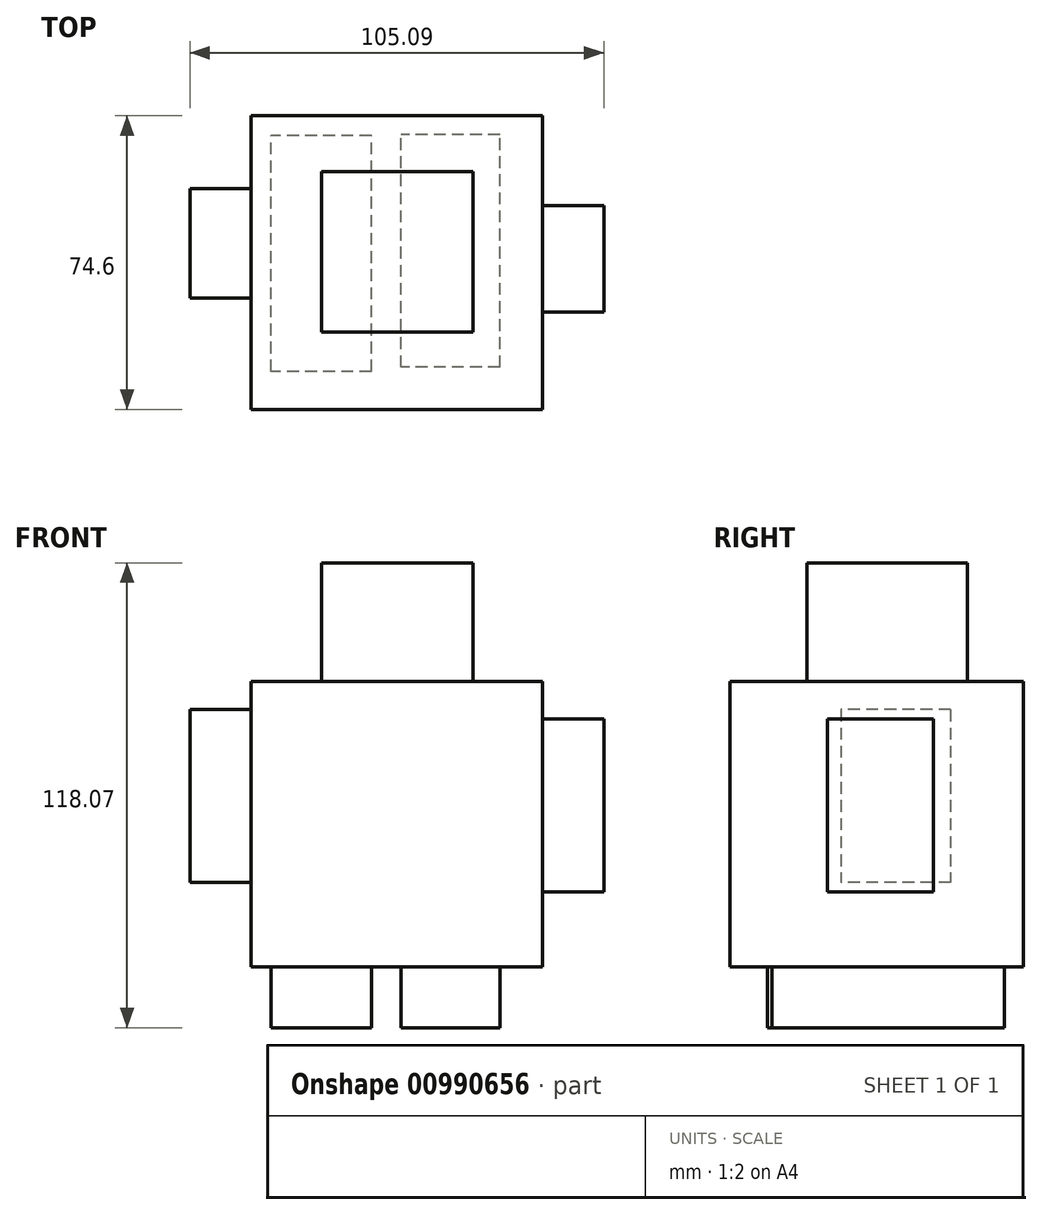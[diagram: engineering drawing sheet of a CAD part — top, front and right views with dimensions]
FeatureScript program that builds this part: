
annotation { "Feature Type Name" : "Feature", "Feature Type Description" : "" }
export const myFeature = defineFeature(function(context is Context, id is Id, definition is map)
    precondition{}
    {
        {
            var Q0;
            Q0=qCreatedBy(makeId("Top.planeOp"),FACE);
            var sketch = newSketch(context, id + "F0", { "sketchPlane" : qUnion([Q0])});
            skLineSegment(sketch, "E0.bottom", {"start": v(0, 0) * mm, "end": v(-74.1, 0) * mm});
            skLineSegment(sketch, "E0.top", {"start": v(0, 74.6) * mm, "end": v(-74.1, 74.6) * mm});
            skLineSegment(sketch, "E0.left", {"start": v(0, 0) * mm, "end": v(0, 74.6) * mm});
            skLineSegment(sketch, "E0.right", {"start": v(-74.1, 0) * mm, "end": v(-74.1, 74.6) * mm});
            skSolve(sketch);
        }
        {
            var Q0;
            Q0 = qSketchRegion(id + "F0", true);
            extrude(context, id + "F1", {"entities" : qUnion([Q0]), "depth" : 72.47 * mm, "offsetDistance" : 25.4 * mm});
        }
        {
            var Q0;
            Q0=makeQuery(id+"F1.opExtrude","CAP_FACE",FACE,{"disambiguationData":[OSD([sQuery(id+"F0.wireOp",EDGE,"E0.bottom"),sQuery(id+"F0.wireOp",EDGE,"E0.top"),sQuery(id+"F0.wireOp",EDGE,"E0.left"),sQuery(id+"F0.wireOp",EDGE,"E0.right")])],"isStart":false});
            var sketch = newSketch(context, id + "F2", { "sketchPlane" : qUnion([Q0])});
            skLineSegment(sketch, "E1.bottom", {"start": v(-56.15, 60.44) * mm, "end": v(-17.76, 60.44) * mm});
            skLineSegment(sketch, "E1.top", {"start": v(-56.15, 19.6) * mm, "end": v(-17.76, 19.6) * mm});
            skLineSegment(sketch, "E1.left", {"start": v(-56.15, 60.44) * mm, "end": v(-56.15, 19.6) * mm});
            skLineSegment(sketch, "E1.right", {"start": v(-17.76, 60.44) * mm, "end": v(-17.76, 19.6) * mm});
            skPoint(sketch, "E1.middle", {"position": v(-36.96, 40.02) * mm});
            skSolve(sketch);
        }
        {
            var Q0;
            Q0 = qSketchRegion(id + "F2", true);
            extrude(context, id + "F3", {"entities" : qUnion([Q0]), "operationType" : NewBodyOperationType.ADD, "depth" : 30.1 * mm, "offsetDistance" : 25 * mm});
        }
        {
            var Q0;
            Q0=makeQuery(id+"F1.opExtrude","SWEPT_FACE",FACE,{"disambiguationData":[OSD([sQuery(id+"F0.wireOp",EDGE,"E0.left")])]});
            var sketch = newSketch(context, id + "F4", { "sketchPlane" : qUnion([Q0])});
            skLineSegment(sketch, "E2.bottom", {"start": v(51.75, 62.92) * mm, "end": v(24.79, 62.92) * mm});
            skLineSegment(sketch, "E2.top", {"start": v(51.75, 19) * mm, "end": v(24.79, 19) * mm});
            skLineSegment(sketch, "E2.left", {"start": v(51.75, 62.92) * mm, "end": v(51.75, 19) * mm});
            skLineSegment(sketch, "E2.right", {"start": v(24.79, 62.92) * mm, "end": v(24.79, 19) * mm});
            skPoint(sketch, "E2.middle", {"position": v(38.27, 40.96) * mm});
            skSolve(sketch);
        }
        {
            var Q0;
            Q0 = qSketchRegion(id + "F4", true);
            extrude(context, id + "F5", {"entities" : qUnion([Q0]), "operationType" : NewBodyOperationType.ADD, "depth" : 15.5 * mm, "offsetDistance" : 25 * mm});
        }
        {
            var Q0;
            Q0=makeQuery(id+"F1.opExtrude","SWEPT_FACE",FACE,{"disambiguationData":[OSD([sQuery(id+"F0.wireOp",EDGE,"E0.right")])]});
            var sketch = newSketch(context, id + "F6", { "sketchPlane" : qUnion([Q0])});
            skLineSegment(sketch, "E3.bottom", {"start": v(-56.1, 65.31) * mm, "end": v(-28.26, 65.31) * mm});
            skLineSegment(sketch, "E3.top", {"start": v(-56.1, 21.4) * mm, "end": v(-28.26, 21.4) * mm});
            skLineSegment(sketch, "E3.left", {"start": v(-56.1, 65.31) * mm, "end": v(-56.1, 21.4) * mm});
            skLineSegment(sketch, "E3.right", {"start": v(-28.26, 65.31) * mm, "end": v(-28.26, 21.4) * mm});
            skPoint(sketch, "E3.middle", {"position": v(-42.18, 43.35) * mm});
            skSolve(sketch);
        }
        {
            var Q0;
            Q0 = qSketchRegion(id + "F6", true);
            extrude(context, id + "F7", {"entities" : qUnion([Q0]), "operationType" : NewBodyOperationType.ADD, "depth" : 15.5 * mm, "offsetDistance" : 25 * mm});
        }
        {
            var Q0;
            Q0=makeQuery(id+"F1.opExtrude","CAP_FACE",FACE,{"disambiguationData":[OSD([sQuery(id+"F0.wireOp",EDGE,"E0.bottom"),sQuery(id+"F0.wireOp",EDGE,"E0.top"),sQuery(id+"F0.wireOp",EDGE,"E0.left"),sQuery(id+"F0.wireOp",EDGE,"E0.right")])],"isStart":true});
            var sketch = newSketch(context, id + "F8", { "sketchPlane" : qUnion([Q0])});
            skLineSegment(sketch, "E4.bottom", {"start": v(-43.56, -9.63) * mm, "end": v(-69.08, -9.63) * mm});
            skLineSegment(sketch, "E4.top", {"start": v(-43.56, -69.62) * mm, "end": v(-69.08, -69.62) * mm});
            skLineSegment(sketch, "E4.left", {"start": v(-43.56, -9.63) * mm, "end": v(-43.56, -69.62) * mm});
            skLineSegment(sketch, "E4.right", {"start": v(-69.08, -9.63) * mm, "end": v(-69.08, -69.62) * mm});
            skPoint(sketch, "E4.middle", {"position": v(-56.32, -39.62) * mm});
            skSolve(sketch);
        }
        {
            var Q0;
            Q0 = qSketchRegion(id + "F8", true);
            extrude(context, id + "F9", {"entities" : qUnion([Q0]), "operationType" : NewBodyOperationType.ADD, "depth" : 15.5 * mm, "offsetDistance" : 25 * mm});
        }
        {
            var Q0;
            Q0=makeQuery(id+"F1.opExtrude","CAP_FACE",FACE,{"disambiguationData":[OSD([sQuery(id+"F0.wireOp",EDGE,"E0.bottom"),sQuery(id+"F0.wireOp",EDGE,"E0.top"),sQuery(id+"F0.wireOp",EDGE,"E0.left"),sQuery(id+"F0.wireOp",EDGE,"E0.right")])],"isStart":true});
            var sketch = newSketch(context, id + "F10", { "sketchPlane" : qUnion([Q0])});
            skLineSegment(sketch, "E5.bottom", {"start": v(-10.88, -10.74) * mm, "end": v(-35.95, -10.74) * mm});
            skLineSegment(sketch, "E5.top", {"start": v(-10.88, -69.84) * mm, "end": v(-35.95, -69.84) * mm});
            skLineSegment(sketch, "E5.left", {"start": v(-10.88, -10.74) * mm, "end": v(-10.88, -69.84) * mm});
            skLineSegment(sketch, "E5.right", {"start": v(-35.95, -10.74) * mm, "end": v(-35.95, -69.84) * mm});
            skPoint(sketch, "E5.middle", {"position": v(-23.41, -40.3) * mm});
            skSolve(sketch);
        }
        {
            var Q0;
            Q0 = qSketchRegion(id + "F10", true);
            extrude(context, id + "F11", {"entities" : qUnion([Q0]), "operationType" : NewBodyOperationType.ADD, "depth" : 15.5 * mm, "offsetDistance" : 25 * mm});
        }
    });
